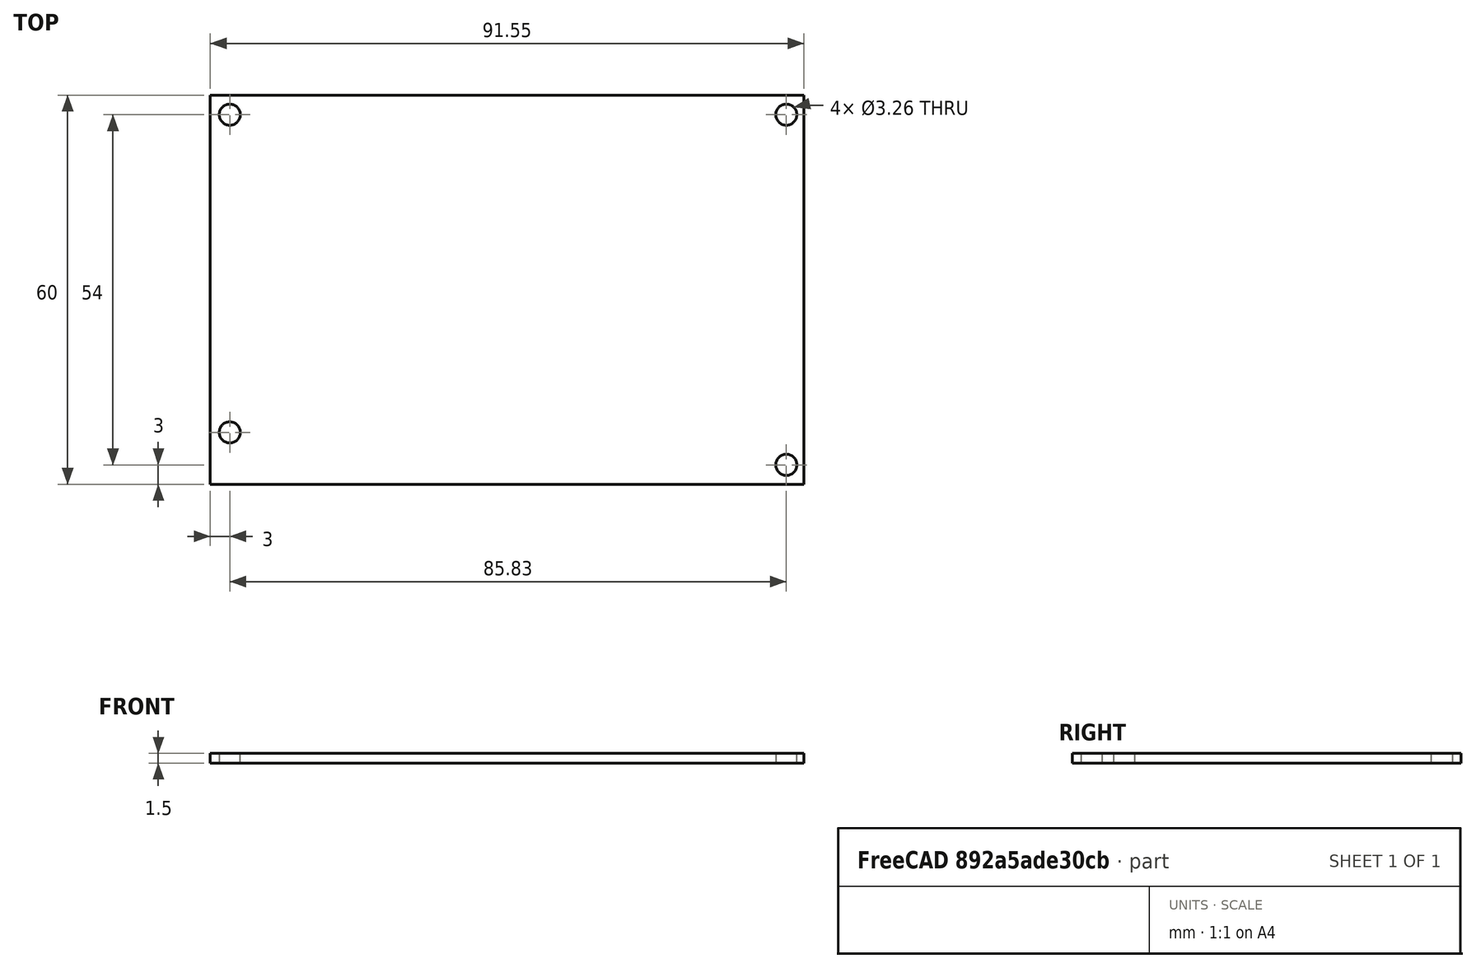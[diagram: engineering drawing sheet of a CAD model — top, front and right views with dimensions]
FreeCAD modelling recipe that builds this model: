
FCSTD DOCUMENT  (FreeCAD 0.15R4664 (Git))
Label: BananaPiCase
License: All rights reserved
LicenseURL: http://en.wikipedia.org/wiki/All_rights_reserved
objects: App::DocumentObjectGroup×1, Sketcher::SketchObject×1, PartDesign::Pad×1
note: 3 computed .brp shape members not serialized (recipe doc carries the construction recipe); baked Part::Feature solids carry a one-line shape summary decoded from their .brp

FEATURE [App::DocumentObjectGroup] Group
FEATURE [Sketcher::SketchObject] Sketch  label="Outline"
  sketch-geometry (15):
    g0: LineSegment StartX=0 StartY=60 StartZ=0 EndX=91.55 EndY=60 EndZ=0
    g1: LineSegment StartX=91.55 StartY=60 StartZ=0 EndX=91.55 EndY=0 EndZ=0
    g2: LineSegment StartX=91.55 StartY=0 StartZ=0 EndX=0 EndY=0 EndZ=0
    g3: LineSegment StartX=0 StartY=0 StartZ=0 EndX=0 EndY=60 EndZ=0
    g4: Circle CenterX=3 CenterY=57 CenterZ=0 NormalX=0 NormalY=0 NormalZ=1 Radius=1.63
    g5: Circle CenterX=3 CenterY=8 CenterZ=0 NormalX=0 NormalY=0 NormalZ=1 Radius=1.63
    g6: Circle CenterX=88.83 CenterY=57 CenterZ=0 NormalX=0 NormalY=0 NormalZ=1 Radius=1.63
    g7: Circle CenterX=88.83 CenterY=3 CenterZ=0 NormalX=0 NormalY=0 NormalZ=1 Radius=1.63
    g8: LineSegment [constr] StartX=88.83 StartY=57 StartZ=0 EndX=88.83 EndY=3 EndZ=0
    g9: LineSegment [constr] StartX=88.83 StartY=57 StartZ=0 EndX=3 EndY=57 EndZ=0
    g10: LineSegment [constr] StartX=3 StartY=8 StartZ=0 EndX=3 EndY=57 EndZ=0
    g11: LineSegment [constr] StartX=3 StartY=57 StartZ=0 EndX=0 EndY=57 EndZ=0
    g12: LineSegment [constr] StartX=3 StartY=57 StartZ=0 EndX=3 EndY=60 EndZ=0
    g13: LineSegment [constr] StartX=88.83 StartY=3 StartZ=0 EndX=88.83 EndY=0 EndZ=0
    g14: LineSegment [constr] StartX=88.83 StartY=3 StartZ=0 EndX=91.55 EndY=3 EndZ=0
  constraints (42):
    c: Coincident(g0,g1)
    c: Coincident(g1,g2)
    c: Coincident(g2,g3)
    c: Coincident(g3,g0)
    c: Horizontal(g0)
    c: Horizontal(g2)
    c: Vertical(g1)
    c: Vertical(g3)
    c: DistanceX(g0) = 91.55
    c: DistanceY(g1) = -60
    c: Radius(g4) = 1.63
    c: Equal(g4,g5)
    c: Equal(g4,g6)
    c: Equal(g4,g7)
    c: Coincident(g8,g6)
    c: Coincident(g8,g7)
    c: Coincident(g9,g6)
    c: Coincident(g9,g4)
    c: Horizontal(g9)
    c: Perpendicular(g8,g9)
    c: DistanceX(g9) = -85.83
    c: DistanceY(g8) = -54
    c: Coincident(g10,g5)
    c: Coincident(g10,g4)
    c: Perpendicular(g10,g9)
    c: DistanceY(g10) = 49
    c: Coincident(g11,g4)
    c: PointOnObject(g11,g3)
    c: Perpendicular(g3,g11)
    c: Coincident(g12,g4)
    c: PointOnObject(g12,g0)
    c: Vertical(g12)
    c: Equal(g12,g11)
    c: Coincident(g13,g7)
    c: PointOnObject(g13,g2)
    c: Vertical(g13)
    c: Coincident(g14,g7)
    c: PointOnObject(g14,g1)
    c: Horizontal(g14)
    c: Equal(g12,g13)
    c: DistanceY(g-1,g2) = 0
    c: DistanceX(g-1,g2) = 0
FEATURE [PartDesign::Pad] Pad
  Length = 1.5
  Length2 = 100
  Sketch = -> Sketch
  Type = 0
